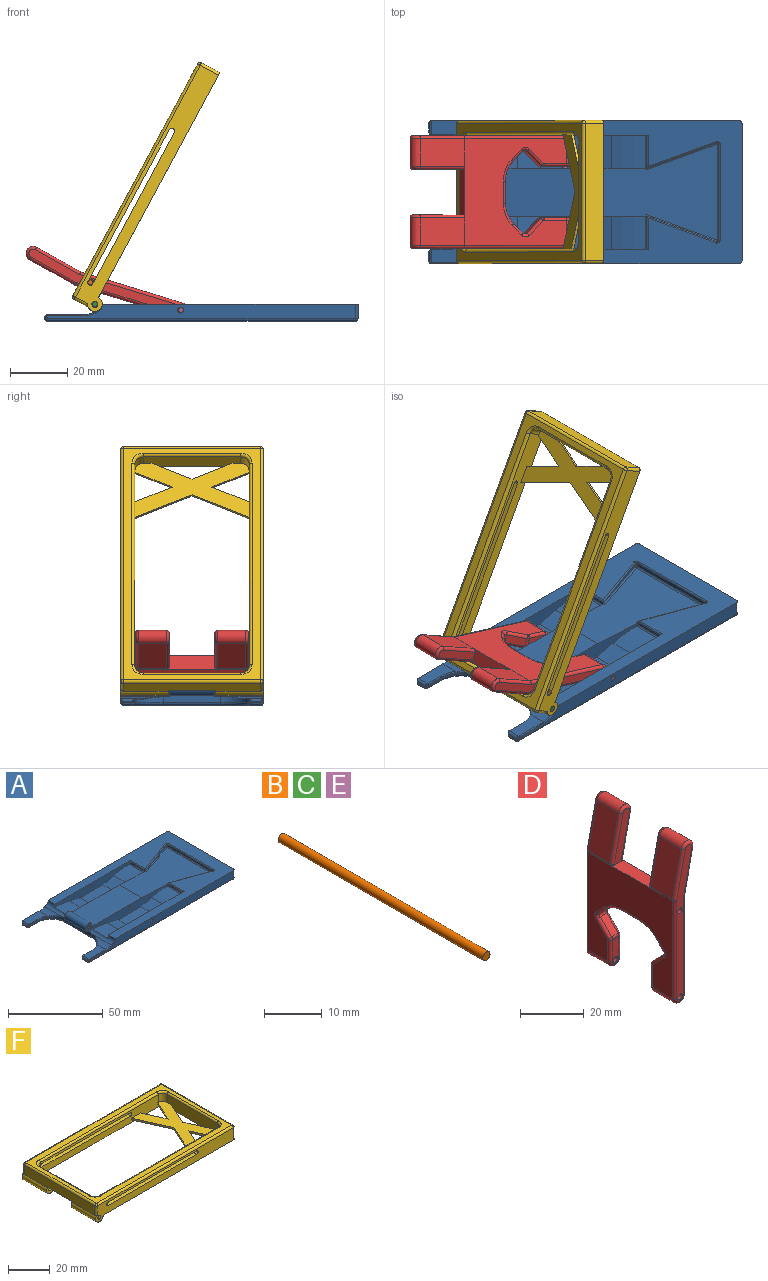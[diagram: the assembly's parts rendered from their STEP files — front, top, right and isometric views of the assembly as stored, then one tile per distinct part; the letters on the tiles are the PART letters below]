
ASSEMBLY  parts=6 mates=6
PART A: 97 faces, bbox 109.8x50.1x8.6 mm
  f0: plane 36.55x16.67mm, normal (0,0,1), area 608.9mm2, adj f6,f15,f21,f32,f33,f34,f35,f42
  f1: plane 20.02x2.47mm, normal (-1,0,0), area 48mm2, adj f15,f32,f33,f34,f35,f46,f48,f66
  f2: plane 57.16x5.5mm, normal (0,1,0), area 220.4mm2, adj f3,f7,f12,f17,f20,f24,f27,f28
  f3: plane 11.67x8.05mm, normal (0.24,0,0.97), area 96.8mm2, adj f2,f20,f21,f28
  f4: plane 11.67x0.11mm, normal (1,0,0), area 1.3mm2, adj f6,f9,f25,f35
  f5: plane 107.5x5mm, normal (0,1,0), area 468.4mm2, adj f7,f16,f35,f39,f47,f86,f91,f95
  f6: plane 56.66x5.5mm, normal (0,1,0), area 210.4mm2, adj f0,f4,f19,f22,f23,f25,f26,f29
  f7: plane 89.25x50mm, normal (0,0,1), area 1520.2mm2, adj f2,f5,f9,f10,f11,f33,f35,f50
  f8: cylinder r=1.05mm len=15.67mm, axis (0,1,0), area 103.4mm2, adj f13,f14,f32,f34
  f9: plane 57.16x5.5mm, normal (0,-1,0), area 220.4mm2, adj f4,f7,f16,f19,f22,f23,f25,f26
  f10: plane 107.5x5mm, normal (0,-1,0), area 462.3mm2, adj f7,f17,f33,f69,f70,f76,f80,f81
  f11: plane 48x5mm, normal (1,0,0), area 240mm2, adj f7,f81,f85,f86
  f12: plane 11.67x0.11mm, normal (1,0,0), area 1.3mm2, adj f2,f21,f28,f33
  f13: plane 5.1x5.1mm, normal (0,-1,0), area 12.7mm2, adj f8,f15,f32
  f14: plane 5.1x5.1mm, normal (0,1,0), area 12.7mm2, adj f8,f15,f34
  f15: cylinder r=2.55mm len=15.67mm, axis (0,1,0), area 188.3mm2, adj f0,f1,f13,f14
  f16: cylinder r=1.05mm len=5mm, axis (0,1,0), area 33mm2, adj f5,f9
  f17: cylinder r=1.05mm len=5mm, axis (0,1,0), area 33mm2, adj f2,f10
  f18: plane 107.5x48mm, normal (0,0,-1), area 4476.9mm2, adj f75,f77,f79,f80,f82,f84,f85,f87
  f19: plane 17x11.67mm, normal (0,0,1), area 198.3mm2, adj f6,f9,f22,f23
  f20: plane 17x11.67mm, normal (0,0,1), area 198.3mm2, adj f2,f3,f21,f24
  f21: plane 56.66x5.5mm, normal (0,-1,0), area 210.4mm2, adj f0,f3,f12,f20,f24,f27,f28,f29
  f22: plane 11.67x8.05mm, normal (0.24,0,0.97), area 96.8mm2, adj f6,f9,f19,f25
  f23: plane 11.67x8.03mm, normal (-0.24,0,0.97), area 96.5mm2, adj f6,f9,f19,f26
  f24: plane 11.67x8.03mm, normal (-0.24,0,0.97), area 96.5mm2, adj f2,f20,f21,f27
  f25: cylinder r=50mm len=11.67mm, axis (0,-1,0), area 135mm2, adj f4,f6,f9,f22
  f26: cylinder r=50mm len=11.67mm, axis (0,-1,0), area 137.1mm2, adj f6,f9,f23,f64
  f27: cylinder r=50mm len=11.67mm, axis (0,-1,0), area 137.1mm2, adj f2,f21,f24,f65
  f28: cylinder r=50mm len=11.67mm, axis (0,-1,0), area 135mm2, adj f2,f3,f12,f21
  f29: cylinder r=1.05mm len=16.67mm, axis (0,-1,0), area 110mm2, adj f6,f21
  f30: plane 12.27x1.09mm, normal (-1,0,0), area 11.7mm2, adj f2,f21,f42,f44,f56,f57,f60,f65
  f31: plane 12.27x1.09mm, normal (-1,0,0), area 11.7mm2, adj f6,f9,f42,f43,f50,f51,f53,f64
  f32: plane 2.75x2.75mm, normal (0,-1,0), area 5.1mm2, adj f0,f1,f8,f13,f33
  f33: cylinder r=2.75mm len=17.17mm, axis (0,-1,0), area 49.6mm2, adj f0,f1,f2,f7,f10,f12,f21,f32
  f34: plane 2.75x2.75mm, normal (0,1,0), area 5.1mm2, adj f0,f1,f8,f14,f35
  f35: cylinder r=2.75mm len=17.17mm, axis (0,1,0), area 49.7mm2, adj f0,f1,f4,f5,f6,f7,f9,f34
  f36: plane 6.5x1.3mm, normal (0,1,0), area 8.4mm2, adj f37,f48,f72,f77
  f37: plane 12.25x6.47mm, normal (0,0,1), area 60.3mm2, adj f36,f48,f49,f69,f71
  f38: plane 3x0.3mm, normal (-1,0,0), area 0.9mm2, adj f71,f72,f75,f76
  f39: plane 12.25x6.39mm, normal (0,0,1), area 60.2mm2, adj f5,f47,f67,f68,f96
  f40: plane 6.5x0.95mm, normal (0,-1,0), area 6.2mm2, adj f46,f68,f87,f92
  f41: plane 3x0.3mm, normal (-1,0,0), area 0.9mm2, adj f90,f92,f95,f96
  f42: plane 44.18x33.57mm, normal (0.05,0,1), area 932.9mm2, adj f0,f6,f21,f30,f31,f51,f57,f58
  f43: cone r=44.74mm half-angle=70deg, axis (0,1,0), area 17.4mm2, adj f31,f51,f52,f53
  f44: cone r=19.56mm half-angle=70deg, axis (0,-1,0), area 17.4mm2, adj f30,f57,f60,f63
  f45: cylinder r=44.74mm len=33.57mm, axis (0,-1,0), area 45.1mm2, adj f52,f58,f59,f63
  f46: cylinder r=10mm len=10mm, axis (0,0,-1), area 20.2mm2, adj f1,f40,f66,f67,f84
  f47: cylinder r=10mm len=12.97mm, axis (0,1,0), area 42.5mm2, adj f5,f35,f39,f66
  f48: cylinder r=10mm len=10mm, axis (0,0,1), area 25mm2, adj f1,f36,f37,f49,f79
  f49: cylinder r=10mm len=14.65mm, axis (0,-1,0), area 46.4mm2, adj f33,f37,f48,f70
  f50: cylinder r=0.5mm len=11.66mm, axis (0,-1,0), area 8.9mm2, adj f7,f9,f31,f53
  f51: bspline ~38.52x14.45mm, area 20.5mm2, adj f31,f42,f43,f54
  f52: torus R=44.24mm, axis (0,-1,0), area 1.3mm2, adj f43,f45,f54,f55
  f53: bspline ~38.15x14.3mm, area 20.4mm2, adj f7,f31,f43,f50,f55
  f54: sphere r=0.5mm, area 0.5mm2, adj f51,f52,f58
  f55: bspline ~1.55x1.16mm, area 1mm2, adj f7,f52,f53,f59
  f56: cylinder r=0.5mm len=11.66mm, axis (0,-1,0), area 8.9mm2, adj f2,f7,f30,f60
  f57: bspline ~38.52x14.45mm, area 20.5mm2, adj f30,f42,f44,f61
  f58: cylinder r=0.5mm len=33.57mm, axis (0,-1,0), area 26.6mm2, adj f42,f45,f54,f61
  f59: cylinder r=0.5mm len=33.57mm, axis (0,-1,0), area 26.2mm2, adj f7,f45,f55,f62
  f60: bspline ~38.15x14.3mm, area 20.4mm2, adj f7,f30,f44,f56,f62
  f61: sphere r=0.5mm, area 0.5mm2, adj f57,f58,f63
  f62: bspline ~1.49x1.22mm, area 1mm2, adj f7,f59,f60,f63
  f63: torus R=44.24mm, axis (0,-1,0), area 1.3mm2, adj f44,f45,f61,f62
  f64: cylinder r=0.5mm len=11.67mm, axis (0,-1,0), area 9.1mm2, adj f6,f9,f26,f31
  f65: cylinder r=0.5mm len=11.67mm, axis (0,-1,0), area 9.1mm2, adj f2,f21,f27,f30
  f66: bspline ~12.69x6.13mm, area 4.9mm2, adj f1,f35,f46,f47,f67
  f67: torus R=10.35mm, axis (0,0,1), area 3.3mm2, adj f39,f46,f66,f68
  f68: cylinder r=0.35mm len=6.5mm, axis (-1,0,0), area 3.6mm2, adj f39,f40,f67,f94
  f69: cylinder r=0.35mm len=12.25mm, axis (-1,0,0), area 6.7mm2, adj f10,f37,f70,f73
  f70: torus R=10.35mm, axis (0,-1,0), area 2.8mm2, adj f10,f33,f49,f69
  f71: cylinder r=1mm len=4.65mm, axis (0,-1,0), area 6mm2, adj f37,f38,f72,f73
  f72: cylinder r=1mm len=1.3mm, axis (0,0,1), area 1.5mm2, adj f36,f38,f71,f74
  f73: bspline ~1.18x1mm, area 0.4mm2, adj f69,f71,f76
  f74: sphere r=1mm, area 2.1mm2, adj f72,f75,f77
  f75: cylinder r=1mm len=3mm, axis (0,-1,0), area 4.7mm2, adj f18,f38,f74,f78
  f76: cylinder r=1mm len=1mm, axis (0,0,-1), area 1mm2, adj f10,f38,f73,f78
  f77: cylinder r=1mm len=6.5mm, axis (1,0,0), area 10.2mm2, adj f18,f36,f74,f79
  f78: sphere r=1mm, area 1.6mm2, adj f75,f76,f80
  f79: torus R=11mm, axis (0,0,1), area 25.6mm2, adj f18,f48,f77,f82
  f80: cylinder r=1mm len=107.5mm, axis (1,0,0), area 168.9mm2, adj f10,f18,f78,f83
  f81: cylinder r=1mm len=5mm, axis (0,0,1), area 7.9mm2, adj f7,f10,f11,f83
  f82: cylinder r=1mm len=20mm, axis (0,-1,0), area 31.4mm2, adj f1,f18,f79,f84
  f83: sphere r=1mm, area 1.6mm2, adj f80,f81,f85
  f84: torus R=11mm, axis (0,0,1), area 25.6mm2, adj f18,f46,f82,f87
  f85: cylinder r=1mm len=48mm, axis (0,1,0), area 75.4mm2, adj f11,f18,f83,f88
  f86: cylinder r=1mm len=5mm, axis (0,0,-1), area 7.9mm2, adj f5,f7,f11,f88
  f87: cylinder r=1mm len=6.5mm, axis (1,0,0), area 10.2mm2, adj f18,f40,f84,f89
  f88: sphere r=1mm, area 1mm2, adj f85,f86,f91
  f89: sphere r=1mm, area 1.6mm2, adj f87,f90,f92
  f90: cylinder r=1mm len=3mm, axis (0,-1,0), area 4.7mm2, adj f18,f41,f89,f93
  f91: cylinder r=1mm len=107.5mm, axis (-1,0,0), area 168.9mm2, adj f5,f18,f88,f93
  f92: cylinder r=1mm len=1mm, axis (0,0,-1), area 1mm2, adj f40,f41,f89,f94
  f93: sphere r=1mm, area 2.1mm2, adj f90,f91,f95
  f94: bspline ~1.04x1mm, area 0.4mm2, adj f68,f92,f96
  f95: cylinder r=1mm len=1.3mm, axis (0,0,-1), area 1.5mm2, adj f5,f41,f93,f96
  f96: cylinder r=1mm len=4.65mm, axis (0,1,0), area 6mm2, adj f39,f41,f94,f95
PART B: 3 faces, bbox 1.8x50x1.8 mm
  f0: plane 1.75x1.75mm, normal (0,1,0), area 2.4mm2, adj f1
  f1: cylinder r=0.88mm len=50mm, axis (0,-1,0), area 274.9mm2, adj f0,f2
  f2: plane 1.75x1.75mm, normal (0,-1,0), area 2.4mm2, adj f1
PART C: same geometry as B
PART D: 89 faces, bbox 9.2x39.4x60.5 mm
  f0: plane 37.4x37.35mm, normal (1,0,0), area 857.9mm2, adj f3,f6,f11,f12,f14,f35,f42,f53
  f1: plane 37.62x37.4mm, normal (-1,0,0), area 867.9mm2, adj f4,f6,f8,f12,f14,f31,f38,f56
  f2: plane 17.51x9.7mm, normal (-0.98,0,0.21), area 173.8mm2, adj f4,f5,f34,f51
  f3: plane 17.25x9.7mm, normal (0.98,0,-0.21), area 171.2mm2, adj f0,f5,f37,f49
  f4: cylinder r=2.5mm len=9.7mm, axis (0,1,0), area 5.2mm2, adj f1,f2,f32,f52
  f5: cylinder r=2.5mm len=9.7mm, axis (0,1,0), area 76.2mm2, adj f2,f3,f36,f50
  f6: cylinder r=2.5mm len=8.7mm, axis (0,1,0), area 68.3mm2, adj f0,f1,f33,f83
  f7: cylinder r=1.05mm len=10.7mm, axis (0,1,0), area 70.6mm2, adj f24,f28
  f8: cylinder r=2.5mm len=9.7mm, axis (0,-1,0), area 5.2mm2, adj f1,f9,f39,f48
  f9: plane 17.51x9.7mm, normal (-0.98,0,0.21), area 173.8mm2, adj f8,f10,f41,f47
  f10: cylinder r=2.5mm len=9.7mm, axis (0,-1,0), area 76.2mm2, adj f9,f11,f43,f46
  f11: plane 17.25x9.7mm, normal (0.98,0,-0.21), area 171.2mm2, adj f0,f10,f44,f45
  f12: cylinder r=2.5mm len=8.7mm, axis (0,-1,0), area 68.3mm2, adj f0,f1,f40,f54
  f13: cylinder r=1.05mm len=10.7mm, axis (0,-1,0), area 70.6mm2, adj f22,f29
  f14: plane 18x5mm, normal (0.05,0,1), area 81mm2, adj f0,f1,f26,f27,f45,f48,f49,f52
  f15: plane 7.72x3mm, normal (0,0,-1), area 23.1mm2, adj f18,f19,f69,f72
  f16: plane 3.44x3.44mm, normal (0,-0.71,-0.71), area 14.6mm2, adj f18,f73,f76,f77
  f17: plane 3.44x3.44mm, normal (0,0.71,-0.71), area 14.6mm2, adj f19,f64,f65,f68
  f18: cylinder r=10mm len=7.07mm, axis (-1,0,0), area 23.6mm2, adj f15,f16,f71,f74
  f19: cylinder r=10mm len=7.07mm, axis (1,0,0), area 23.6mm2, adj f15,f17,f67,f70
  f20: plane 5.14x5.14mm, normal (0,0.71,0.71), area 21.8mm2, adj f59,f60,f63,f64
  f21: cylinder r=1mm len=3mm, axis (-1,0,0), area 0.8mm2, adj f22,f55,f58,f59
  f22: plane 9.57x3mm, normal (0,1,0), area 24.3mm2, adj f13,f21,f53,f54,f56
  f23: plane 5.14x5.14mm, normal (0,-0.71,0.71), area 21.8mm2, adj f77,f78,f84,f85
  f24: plane 9.57x3mm, normal (0,-1,0), area 24.3mm2, adj f7,f25,f80,f83,f86
  f25: cylinder r=1mm len=3mm, axis (1,0,0), area 0.8mm2, adj f24,f79,f85,f88
  f26: plane 19.22x6.8mm, normal (0,1,0), area 57.7mm2, adj f14,f45,f46,f47,f48
  f27: plane 19.22x6.8mm, normal (0,-1,0), area 57.7mm2, adj f14,f49,f50,f51,f52
  f28: plane 58.13x6.8mm, normal (0,1,0), area 166.7mm2, adj f7,f30,f31,f32,f33,f34,f35,f36
  f29: plane 58.13x6.8mm, normal (0,-1,0), area 166.7mm2, adj f13,f30,f38,f39,f40,f41,f42,f43
  f30: cylinder r=1.05mm len=39.4mm, axis (0,-1,0), area 259.9mm2, adj f28,f29
  f31: cylinder r=1mm len=37.62mm, axis (0,0,1), area 59.1mm2, adj f1,f28,f32,f33
  f32: torus R=1.5mm, axis (0,-1,0), area 0.7mm2, adj f4,f28,f31,f34
  f33: torus R=1.5mm, axis (0,-1,0), area 10.5mm2, adj f6,f28,f31,f35
  f34: cylinder r=1mm len=17.72mm, axis (0.21,0,0.98), area 28.1mm2, adj f2,f28,f32,f36
  f35: cylinder r=1mm len=37.45mm, axis (0,0,-1), area 58.7mm2, adj f0,f28,f33,f37
  f36: torus R=1.5mm, axis (0,-1,0), area 10.5mm2, adj f5,f28,f34,f37
  f37: cylinder r=1mm len=17.57mm, axis (-0.21,0,-0.98), area 27.8mm2, adj f3,f28,f35,f36
  f38: cylinder r=1mm len=37.62mm, axis (0,0,1), area 59.1mm2, adj f1,f29,f39,f40
  f39: torus R=1.5mm, axis (0,1,0), area 0.7mm2, adj f8,f29,f38,f41
  f40: torus R=1.5mm, axis (0,1,0), area 10.5mm2, adj f12,f29,f38,f42
  f41: cylinder r=1mm len=17.72mm, axis (0.21,0,0.98), area 28.1mm2, adj f9,f29,f39,f43
  f42: cylinder r=1mm len=37.45mm, axis (0,0,-1), area 58.7mm2, adj f0,f29,f40,f44
  f43: torus R=1.5mm, axis (0,1,0), area 10.5mm2, adj f10,f29,f41,f44
  f44: cylinder r=1mm len=17.57mm, axis (-0.21,0,-0.98), area 27.8mm2, adj f11,f29,f42,f43
  f45: cylinder r=1mm len=17.62mm, axis (0.21,0,0.98), area 27.8mm2, adj f11,f14,f26,f46
  f46: torus R=1.5mm, axis (0,1,0), area 10.5mm2, adj f10,f26,f45,f47
  f47: cylinder r=1mm len=17.72mm, axis (-0.21,0,-0.98), area 28.1mm2, adj f9,f26,f46,f48
  f48: torus R=1.5mm, axis (0,1,0), area 0.7mm2, adj f8,f14,f26,f47
  f49: cylinder r=1mm len=17.62mm, axis (0.21,0,0.98), area 27.8mm2, adj f3,f14,f27,f50
  f50: torus R=1.5mm, axis (0,-1,0), area 10.5mm2, adj f5,f27,f49,f51
  f51: cylinder r=1mm len=17.72mm, axis (-0.21,0,-0.98), area 28.1mm2, adj f2,f27,f50,f52
  f52: torus R=1.5mm, axis (0,-1,0), area 0.7mm2, adj f4,f14,f27,f51
  f53: cylinder r=1mm len=8.07mm, axis (0,0,1), area 12.7mm2, adj f0,f22,f54,f55
  f54: torus R=1.5mm, axis (0,1,0), area 10.5mm2, adj f12,f22,f53,f56
  f55: torus R=2mm, axis (1,0,0), area 0.6mm2, adj f0,f21,f53,f57
  f56: cylinder r=1mm len=8.07mm, axis (0,0,-1), area 12.7mm2, adj f1,f22,f54,f58
  f57: sphere r=1mm, area 1mm2, adj f55,f59,f60
  f58: torus R=2mm, axis (1,0,0), area 0.6mm2, adj f1,f21,f56,f61
  f59: cylinder r=1mm len=3mm, axis (-1,0,0), area 3.1mm2, adj f20,f21,f57,f61
  f60: cylinder r=1mm len=5.85mm, axis (0,-0.71,0.71), area 11.4mm2, adj f0,f20,f57,f62
  f61: sphere r=1mm, area 1mm2, adj f58,f59,f63
  f62: torus R=2mm, axis (1,0,0), area 3.4mm2, adj f0,f60,f64,f65
  f63: cylinder r=1mm len=5.85mm, axis (0,0.71,-0.71), area 11.4mm2, adj f1,f20,f61,f66
  f64: cylinder r=1mm len=3mm, axis (-1,0,0), area 4.7mm2, adj f17,f20,f62,f66
  f65: cylinder r=1mm len=4.14mm, axis (0,0.71,0.71), area 7.6mm2, adj f0,f17,f62,f67
  f66: torus R=2mm, axis (1,0,0), area 3.4mm2, adj f1,f63,f64,f68
  f67: torus R=11mm, axis (1,0,0), area 12.8mm2, adj f0,f19,f65,f69
  f68: cylinder r=1mm len=4.14mm, axis (0,0.71,0.71), area 7.6mm2, adj f1,f17,f66,f70
  f69: cylinder r=1mm len=7.72mm, axis (0,1,0), area 12.1mm2, adj f0,f15,f67,f71
  f70: torus R=11mm, axis (1,0,0), area 12.8mm2, adj f1,f19,f68,f72
  f71: torus R=11mm, axis (1,0,0), area 12.8mm2, adj f0,f18,f69,f73
  f72: cylinder r=1mm len=7.72mm, axis (0,-1,0), area 12.1mm2, adj f1,f15,f70,f74
  f73: cylinder r=1mm len=4.14mm, axis (0,0.71,-0.71), area 7.6mm2, adj f0,f16,f71,f75
  f74: torus R=11mm, axis (1,0,0), area 12.8mm2, adj f1,f18,f72,f76
  f75: torus R=2mm, axis (1,0,0), area 3.4mm2, adj f0,f73,f77,f78
  f76: cylinder r=1mm len=4.14mm, axis (0,0.71,-0.71), area 7.6mm2, adj f1,f16,f74,f81
  f77: cylinder r=1mm len=3mm, axis (1,0,0), area 4.7mm2, adj f16,f23,f75,f81
  f78: cylinder r=1mm len=5.85mm, axis (0,0.71,0.71), area 11.4mm2, adj f0,f23,f75,f82
  f79: torus R=2mm, axis (1,0,0), area 0.6mm2, adj f0,f25,f80,f82
  f80: cylinder r=1mm len=8.07mm, axis (0,0,1), area 12.7mm2, adj f0,f24,f79,f83
  f81: torus R=2mm, axis (1,0,0), area 3.4mm2, adj f1,f76,f77,f84
  f82: sphere r=1mm, area 1mm2, adj f78,f79,f85
  f83: torus R=1.5mm, axis (0,-1,0), area 10.5mm2, adj f6,f24,f80,f86
  f84: cylinder r=1mm len=5.85mm, axis (0,-0.71,-0.71), area 11.4mm2, adj f1,f23,f81,f87
  f85: cylinder r=1mm len=3mm, axis (1,0,0), area 3.1mm2, adj f23,f25,f82,f87
  f86: cylinder r=1mm len=8.07mm, axis (0,0,-1), area 12.7mm2, adj f1,f24,f83,f88
  f87: sphere r=1mm, area 1mm2, adj f84,f85,f88
  f88: torus R=2mm, axis (1,0,0), area 0.6mm2, adj f1,f25,f86,f87
PART E: same geometry as B
PART F: 61 faces, bbox 94.6x50x10.8 mm
  f0: cylinder r=1.05mm len=16.67mm, axis (0,-1,0), area 110mm2, adj f9,f17
  f1: plane 34x5.63mm, normal (1,0,0), area 183.9mm2, adj f14,f15,f16,f17,f35,f38,f58,f60
  f2: plane 40x21.5mm, normal (0,0,1), area 435mm2, adj f3,f5,f6,f7,f11,f27,f28,f29
  f3: plane 13.07x5.88mm, normal (-0.91,-0.41,0), area 14.3mm2, adj f2,f4,f7,f29
  f4: plane 40x21.5mm, normal (0,0,-1), area 435mm2, adj f3,f5,f6,f7,f11,f27,f28,f29
  f5: plane 13.07x5.88mm, normal (-0.91,0.41,0), area 14.3mm2, adj f2,f4,f6,f32
  f6: plane 80x7.21mm, normal (0,-1,0), area 447mm2, adj f2,f4,f5,f12,f18,f19,f20,f21
  f7: plane 80x7.21mm, normal (0,1,0), area 447mm2, adj f2,f3,f4,f12,f22,f23,f24,f25
  f8: plane 93.55x9.76mm, normal (0,-1,0), area 549.6mm2, adj f12,f13,f14,f22,f23,f24,f25,f40
  f9: plane 93.55x9.76mm, normal (0,1,0), area 549.6mm2, adj f0,f12,f16,f18,f19,f20,f21,f42
  f10: plane 48x7.21mm, normal (1,0,0), area 346.1mm2, adj f12,f40,f42,f43
  f11: plane 34x7.21mm, normal (-1,0,0), area 239.1mm2, adj f2,f4,f12,f30,f31,f33,f34,f36
  f12: plane 89.45x50mm, normal (0,0,-1), area 1059.8mm2, adj f6,f7,f8,f9,f10,f11,f14,f16
  f13: cylinder r=1.05mm len=16.67mm, axis (0,-1,0), area 110mm2, adj f8,f15
  f14: cylinder r=2.55mm len=16.67mm, axis (0,-1,0), area 179.4mm2, adj f1,f8,f12,f15,f38,f39,f45
  f15: plane 5.4x5.1mm, normal (0,1,0), area 18.3mm2, adj f1,f13,f14,f39,f60
  f16: cylinder r=2.55mm len=16.67mm, axis (0,1,0), area 179.4mm2, adj f1,f9,f12,f17,f35,f39,f51
  f17: plane 5.4x5.1mm, normal (0,-1,0), area 18.3mm2, adj f0,f1,f16,f39,f60
  f18: plane 60x5mm, normal (0,0,1), area 300mm2, adj f6,f9,f19,f21
  f19: cylinder r=1mm len=5mm, axis (0,-1,0), area 15.7mm2, adj f6,f9,f18,f20
  f20: plane 60x5mm, normal (0,0,-1), area 300mm2, adj f6,f9,f19,f21
  f21: cylinder r=1mm len=5mm, axis (0,-1,0), area 15.7mm2, adj f6,f9,f18,f20
  f22: cylinder r=1mm len=5mm, axis (0,-1,0), area 15.7mm2, adj f7,f8,f23,f25
  f23: plane 60x5mm, normal (0,0,-1), area 300mm2, adj f7,f8,f22,f24
  f24: cylinder r=1mm len=5mm, axis (0,-1,0), area 15.7mm2, adj f7,f8,f23,f25
  f25: plane 60x5mm, normal (0,0,1), area 300mm2, adj f7,f8,f22,f24
  f26: plane 92x48mm, normal (0,0,1), area 733.7mm2, adj f43,f44,f48,f49,f52,f53,f54,f55
  f27: plane 20x8.99mm, normal (-0.91,-0.41,0), area 21.9mm2, adj f2,f4,f6,f28
  f28: plane 20x8.99mm, normal (-0.91,0.41,0), area 21.9mm2, adj f2,f4,f7,f27
  f29: plane 13.07x5.88mm, normal (0.91,-0.41,0), area 14.3mm2, adj f2,f3,f4,f7
  f30: plane 13.98x6.28mm, normal (0.91,0.41,0), area 15.3mm2, adj f2,f4,f11,f31
  f31: plane 13.98x6.28mm, normal (0.91,-0.41,0), area 15.3mm2, adj f2,f4,f11,f30
  f32: plane 13.07x5.88mm, normal (0.91,0.41,0), area 14.3mm2, adj f2,f4,f5,f6
  f33: cylinder r=3mm len=4.71mm, axis (0,0,1), area 22.2mm2, adj f2,f7,f11,f55
  f34: cylinder r=3mm len=3mm, axis (0,0,-1), area 7.1mm2, adj f4,f6,f11,f12
  f35: cylinder r=3mm len=7.21mm, axis (0,0,1), area 31.7mm2, adj f1,f6,f12,f16,f56
  f36: cylinder r=3mm len=4.71mm, axis (0,0,-1), area 22.2mm2, adj f2,f6,f11,f52
  f37: cylinder r=3mm len=3mm, axis (0,0,1), area 7.1mm2, adj f4,f7,f11,f12
  f38: cylinder r=3mm len=7.21mm, axis (0,0,-1), area 31.7mm2, adj f1,f7,f12,f14,f59
  f39: plane 48x5.63mm, normal (-1,0,0), area 262.7mm2, adj f14,f15,f16,f17,f45,f49,f51,f60
  f40: cylinder r=1mm len=7.21mm, axis (0,0,-1), area 11.3mm2, adj f8,f10,f12,f41
  f41: sphere r=1mm, area 1.6mm2, adj f40,f43,f44
  f42: cylinder r=1mm len=7.21mm, axis (0,0,1), area 11.3mm2, adj f9,f10,f12,f46
  f43: cylinder r=1mm len=48mm, axis (0,1,0), area 75.4mm2, adj f10,f26,f41,f46
  f44: cylinder r=1mm len=92mm, axis (1,0,0), area 144.5mm2, adj f8,f26,f41,f47
  f45: cylinder r=1mm len=5.63mm, axis (0,0,1), area 8.3mm2, adj f8,f14,f39,f47
  f46: sphere r=1mm, area 1.6mm2, adj f42,f43,f48
  f47: sphere r=1mm, area 1.6mm2, adj f44,f45,f49
  f48: cylinder r=1mm len=92mm, axis (-1,0,0), area 144.5mm2, adj f9,f26,f46,f50
  f49: cylinder r=1mm len=48mm, axis (0,-1,0), area 75.4mm2, adj f26,f39,f47,f50
  f50: sphere r=1mm, area 1.6mm2, adj f48,f49,f51
  f51: cylinder r=1mm len=5.63mm, axis (0,0,-1), area 8.3mm2, adj f9,f16,f39,f50
  f52: torus R=4mm, axis (0,0,-1), area 8.3mm2, adj f26,f36,f53,f54
  f53: cylinder r=1mm len=34mm, axis (0,-1,0), area 53.4mm2, adj f11,f26,f52,f55
  f54: cylinder r=1mm len=80mm, axis (1,0,0), area 125.7mm2, adj f6,f26,f52,f56
  f55: torus R=4mm, axis (0,0,-1), area 8.3mm2, adj f26,f33,f53,f57
  f56: torus R=4mm, axis (0,0,-1), area 8.3mm2, adj f26,f35,f54,f58
  f57: cylinder r=1mm len=80mm, axis (1,0,0), area 125.7mm2, adj f7,f26,f55,f59
  f58: cylinder r=1mm len=34mm, axis (0,-1,0), area 53.4mm2, adj f1,f26,f56,f59
  f59: torus R=4mm, axis (0,0,-1), area 8.3mm2, adj f26,f38,f57,f58
  f60: cylinder r=2.85mm len=16.67mm, axis (0,-1,0), area 73.9mm2, adj f1,f15,f17,f39
PLACE A t=(3.76,7.45,7.92)mm fixed
PLACE B rot(axis=(0,-1,0),109.4deg) t=(-36.42,7.45,52.7)mm
PLACE C rot(axis=(0,1,0),28.3deg) t=(-27.7,7.45,-6.44)mm
PLACE D rot(axis=(0,-1,0),73deg) t=(0.8,7.45,27.92)mm
PLACE E t=(12.23,7.45,0.89)mm
PLACE F rot(axis=(0,-1,0),61.7deg) t=(-12.41,7.45,53.51)mm
MATE revolute A.f8 <-> F.f0  axis (0,-1,0) through (-41.24,-0.38,17.92)mm
MATE revolute D.f6 <-> E.f1  axis (0,-1,0) through (-11.24,-12.25,15.92)mm
MATE fastened E.f1 <-> A.f16  axis (0,-1,0) through (-11.24,-17.55,15.92)mm
MATE fastened C.f1 <-> F.f0  axis (0,-1,0) through (-41.24,-17.55,17.92)mm
MATE revolute B.f1 <-> D.f30  axis (0,-1,0) through (-42.79,-17.55,25.57)mm
MATE pin_slot B.f1 <-> F.f19  axis (0,-1,0) through (-42.79,-17.55,25.57)mm
